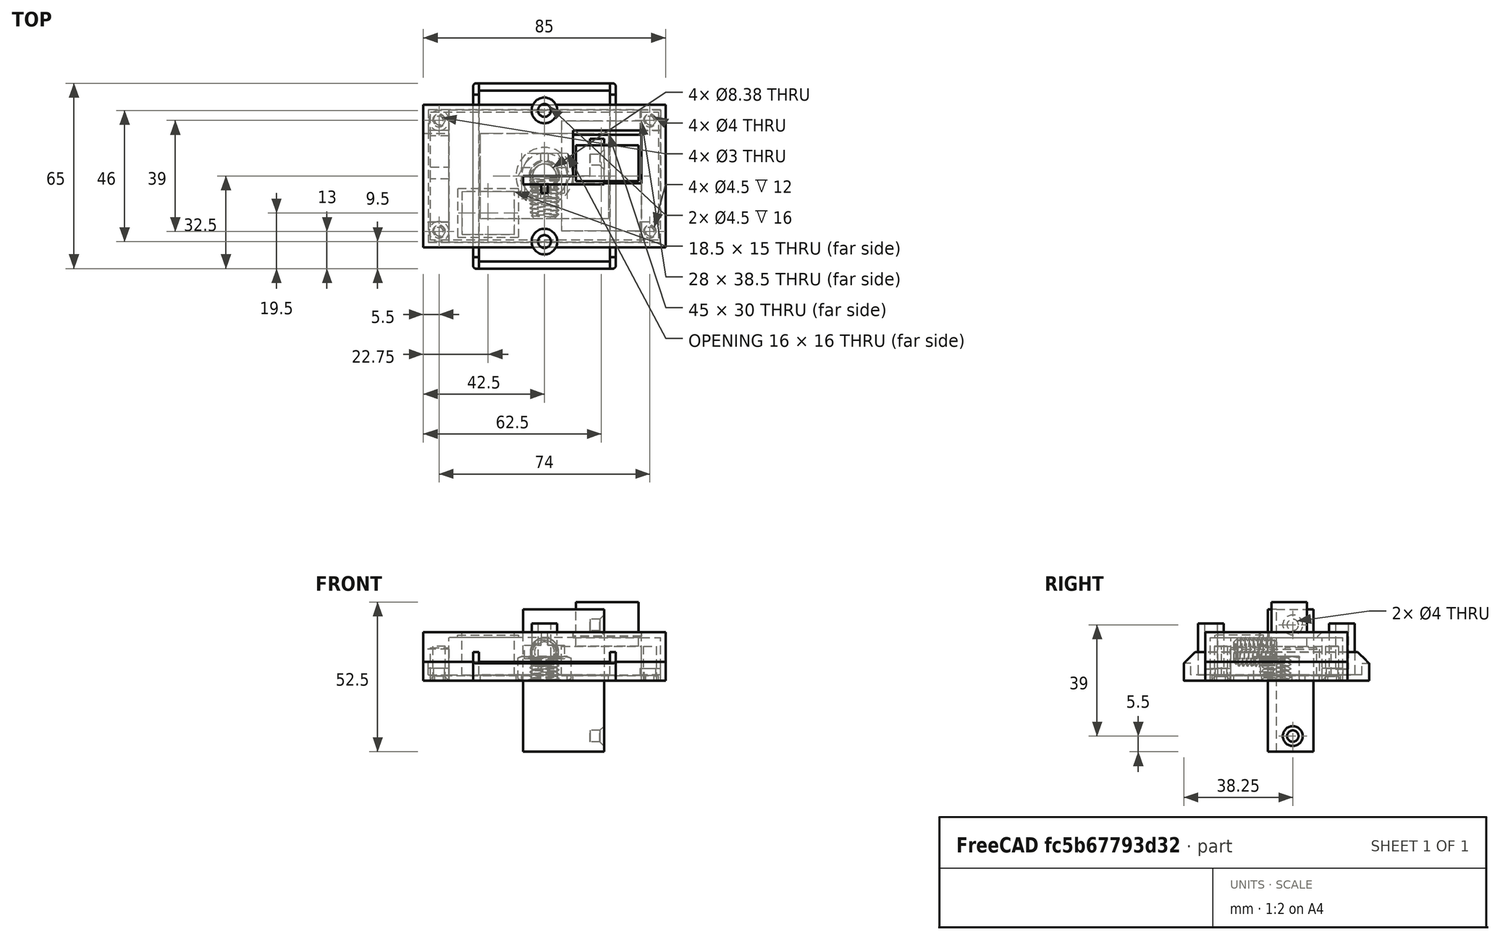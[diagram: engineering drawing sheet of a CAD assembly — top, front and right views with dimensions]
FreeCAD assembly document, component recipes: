
FREECAD ASSEMBLY — COMPONENT RECIPES ("case")

This assembly document has 6 components, labeled P0..P5 below (a component is one placed body or linked part). 6 of them carry a construction recipe — the FreeCAD feature program that regenerates the part from scratch, quoted from this document or its linked companion documents; the rest are supplied as boundary geometry only. No exploded tour is included for this assembly.
COMPONENT P0 — recipe-attached ("Base", modeled in this document).
Construction recipe (the document's own serialized feature program — sketch geometry with constraints, then the solid features built on it; lengths are millimeters unless a unit is written):

FEATURE [PartDesign::CoordinateSystem] LCS_002
  AttacherType = Attacher::AttachEngine3D
  MapMode = 2
  Support = -> [X_Axis003]
FEATURE [Sketcher::SketchObject] Sketch007
  FullyConstrained = true
  MapMode = 5
  Support = -> [XY_Plane003]
  sketch-geometry (4):
    g0: LineSegment StartX=-42.5 StartY=25 StartZ=0 EndX=42.5 EndY=25 EndZ=0
    g1: LineSegment StartX=42.5 StartY=25 StartZ=0 EndX=42.5 EndY=-25 EndZ=0
    g2: LineSegment StartX=42.5 StartY=-25 StartZ=0 EndX=-42.5 EndY=-25 EndZ=0
    g3: LineSegment StartX=-42.5 StartY=-25 StartZ=0 EndX=-42.5 EndY=25 EndZ=0
  constraints (10):
    c: Horizontal(g0)
    c: Vertical(g1)
    c: Coincident(g2,g1)
    c: Coincident(g3,g2)
    c: Coincident(g0,g3)
    c: DistanceX(g2,g2) = 85
    c: DistanceY(g3,g3) = 50
    c: Symmetric(g1,g2,g-2)
    c: Symmetric(g0,g2,g-1)
    c: Coincident(g0,g1)
FEATURE [PartDesign::Pad] Pad006
  Direction = (0,0,1)
  Length = 6.5
  Length2 = 10
  Profile = -> Sketch007
  ReferenceAxis = -> Sketch007 [N_Axis]
  Type = 0
FEATURE [PartDesign::CoordinateSystem] Local_CS004  label="MainboardMount"
  AttacherType = Attacher::AttachEngine3D
  AttachmentOffset = pos=(0,0,4.5) rot=(0,0,1;0rad)
  MapMode = 5
  Placement = pos=(0,0,4.5) rot=(0,0,1;0rad)
  Support = -> [LCS_002]
FEATURE [Sketcher::SketchObject] Sketch008
  AttachmentOffset = pos=(0,0,2) rot=(0,0,1;0rad)
  FullyConstrained = true
  MapMode = 5
  Placement = pos=(0,0,2) rot=(0,0,1;0rad)
  Support = -> [XY_Plane003]
  sketch-geometry (4):
    g0: LineSegment StartX=-40.75 StartY=23.25 StartZ=0 EndX=40.75 EndY=23.25 EndZ=0
    g1: LineSegment StartX=40.75 StartY=23.25 StartZ=0 EndX=40.75 EndY=-23.25 EndZ=0
    g2: LineSegment StartX=40.75 StartY=-23.25 StartZ=0 EndX=-40.75 EndY=-23.25 EndZ=0
    g3: LineSegment StartX=-40.75 StartY=-23.25 StartZ=0 EndX=-40.75 EndY=23.25 EndZ=0
  constraints (10):
    c: Coincident(g0,g1)
    c: Coincident(g1,g2)
    c: Coincident(g2,g3)
    c: Coincident(g3,g0)
    c: Horizontal(g2)
    c: Vertical(g3)
    c: DistanceX(g0,g0) = 81.5
    c: DistanceY(g1,g1) = 46.5
    c: Symmetric(g0,g1,g-1)
    c: Symmetric(g0,g0,g-2)
FEATURE [PartDesign::Pocket] Pocket
  BaseFeature = -> Pad006
  Direction = (0,0,-1)
  Length = 5
  Length2 = 5
  Profile = -> Sketch008
  ReferenceAxis = -> Sketch008 [N_Axis]
  Reversed = true
  Type = 1
FEATURE [Sketcher::SketchObject] Sketch010
  FullyConstrained = true
  MapMode = 5
  Support = -> [XY_Plane003]
  sketch-geometry (4):
    g0: LineSegment StartX=-33.5 StartY=-16 StartZ=0 EndX=-42.5 EndY=-16 EndZ=0
    g1: LineSegment StartX=-42.5 StartY=-16 StartZ=0 EndX=-42.5 EndY=-25 EndZ=0
    g2: LineSegment StartX=-42.5 StartY=-25 StartZ=0 EndX=-33.5 EndY=-25 EndZ=0
    g3: LineSegment StartX=-33.5 StartY=-25 StartZ=0 EndX=-33.5 EndY=-16 EndZ=0
  constraints (12):
    c: Coincident(g0,g1)
    c: Coincident(g1,g2)
    c: Coincident(g2,g3)
    c: Coincident(g3,g0)
    c: Horizontal(g0)
    c: Horizontal(g2)
    c: Vertical(g1)
    c: Vertical(g3)
    c: DistanceX(g0,g-1) = 33.5
    c: DistanceY(g0,g-1) = 16
    c: DistanceX(g2,g2) = 9
    c: DistanceY(g1,g1) = 9
FEATURE [PartDesign::Pad] Pad007
  BaseFeature = -> Pocket
  Direction = (0,0,1)
  Length = 4.3
  Length2 = 10
  Profile = -> Sketch010
  ReferenceAxis = -> Sketch010 [N_Axis]
  Type = 0
FEATURE [PartDesign::Mirrored] Mirrored002
  MirrorPlane = -> Sketch010 [V_Axis]
FEATURE [PartDesign::Mirrored] Mirrored003
  MirrorPlane = -> Sketch010 [H_Axis]
FEATURE [PartDesign::MultiTransform] MultiTransform001
  BaseFeature = -> Pad007
  Originals = -> [Pad007]
  Transformations = -> [Mirrored002,Mirrored003]
FEATURE [PartDesign::SubtractiveCylinder] Cylinder001
  Angle = 360
  AttacherType = Attacher::AttachEngine3D
  AttachmentOffset = pos=(-37,-19.5,0) rot=(0,0,1;0rad)
  BaseFeature = -> MultiTransform001
  FirstAngle = 0
  Height = 10
  MapMode = 5
  Placement = pos=(-37,-19.5,0) rot=(0,0,1;0rad)
  Radius = 2
  SecondAngle = 0
  Support = -> [XY_Plane003]
  expr: Radius = 2
FEATURE [PartDesign::Mirrored] Mirrored004
  MirrorPlane = -> YZ_Plane003
  Placement = pos=(-37,-19.5,0) rot=(0,0,1;0rad)
FEATURE [PartDesign::Mirrored] Mirrored005
  MirrorPlane = -> XZ_Plane003
  Placement = pos=(-37,-19.5,0) rot=(0,0,1;0rad)
FEATURE [PartDesign::MultiTransform] MultiTransform002
  BaseFeature = -> Cylinder001
  Originals = -> [Cylinder001]
  Placement = pos=(-37,-19.5,0) rot=(0,0,1;0rad)
  Transformations = -> [Mirrored004,Mirrored005]
FEATURE [PartDesign::CoordinateSystem] Local_CS006  label="TopMount"
  AttacherType = Attacher::AttachEngine3D
  AttachmentOffset = pos=(0,0,6.5) rot=(0,0,1;0rad)
  MapMode = 5
  Placement = pos=(0,0,6.5) rot=(0,0,1;0rad)
  Support = -> [LCS_002]
FEATURE [Sketcher::SketchObject] Sketch017
  AttachmentOffset = pos=(0,0,6.5) rot=(0,0,1;0rad)
  FullyConstrained = false
  MapMode = 5
  Placement = pos=(0,0,6.5) rot=(0,0,1;0rad)
  Support = -> [XY_Plane003]
  sketch-geometry (4):
    g0: LineSegment StartX=-43.7107 StartY=16 StartZ=0 EndX=-39.4081 EndY=16 EndZ=0
    g1: LineSegment StartX=-39.4081 StartY=16 StartZ=0 EndX=-39.4081 EndY=-16 EndZ=0
    g2: LineSegment StartX=-39.4081 StartY=-16 StartZ=0 EndX=-43.7107 EndY=-16 EndZ=0
    g3: LineSegment StartX=-43.7107 StartY=-16 StartZ=0 EndX=-43.7107 EndY=16 EndZ=0
  constraints (9):
    c: Coincident(g0,g1)
    c: Coincident(g1,g2)
    c: Coincident(g2,g3)
    c: Coincident(g3,g0)
    c: Horizontal(g0)
    c: Horizontal(g2)
    c: Vertical(g1)
    c: DistanceY(g3,g3) = 32
    c: Symmetric(g0,g2,g-1)
FEATURE [PartDesign::Pocket] Pocket006
  BaseFeature = -> MultiTransform002
  Direction = (0,0,-1)
  Length = 5
  Length2 = 5
  Placement = pos=(-37,-19.5,0) rot=(0,0,1;0rad)
  Profile = -> Sketch017
  ReferenceAxis = -> Sketch017 [N_Axis]
  Reversed = true
  Type = 0
FEATURE [PartDesign::Chamfer] Chamfer
  Angle = 45
  Base = -> Pocket006 [Edge62,Edge8]
  BaseFeature = -> Pocket006
  ChamferType = 0
  FlipDirection = false
  Placement = pos=(-37,-19.5,0) rot=(0,0,1;0rad)
  Size = 1.5
  Size2 = 1
  SupportTransform = false
  UseAllEdges = false
FEATURE [PartDesign::CoordinateSystem] Local_CS008  label="ScrewBase"
  AttacherType = Attacher::AttachEngine3D
  AttachmentOffset = pos=(-1,2,0) rot=(0,0,1;0rad)
  MapMode = 45
  Placement = pos=(43.5,4e-16,2) rot=(0,0.707107,0.707107;3.14159rad)
  Support = -> [Chamfer]
FEATURE [PartDesign::Body] Base
  Group = -> [LCS_002,Sketch007,Pad006,Local_CS004,Sketch008,Sketch010,Pocket,Pad007,MultiTransform001,Mirrored002,Mirrored003,Cylinder001,MultiTransform002,Mirrored004,Mirrored005,Local_CS006,Sketch017,Pocket006,Local_CS008,Chamfer]
  Origin = -> Origin003
  Tip = -> Chamfer
COMPONENT P1 — recipe-attached ("Mainboard", modeled in this document).
Construction recipe (the document's own serialized feature program — sketch geometry with constraints, then the solid features built on it; lengths are millimeters unless a unit is written):

FEATURE [PartDesign::CoordinateSystem] LCS_0
  AttacherType = Attacher::AttachEngine3D
  MapMode = 2
  Support = -> [X_Axis001]
FEATURE [Sketcher::SketchObject] Sketch
  FullyConstrained = true
  MapMode = 5
  Support = -> [XY_Plane001]
  sketch-geometry (4):
    g0: LineSegment StartX=-40 StartY=22.5 StartZ=0 EndX=40 EndY=22.5 EndZ=0
    g1: LineSegment StartX=40 StartY=22.5 StartZ=0 EndX=40 EndY=-22.5 EndZ=0
    g2: LineSegment StartX=40 StartY=-22.5 StartZ=0 EndX=-40 EndY=-22.5 EndZ=0
    g3: LineSegment StartX=-40 StartY=-22.5 StartZ=0 EndX=-40 EndY=22.5 EndZ=0
  constraints (10):
    c: Coincident(g0,g1)
    c: Coincident(g1,g2)
    c: Coincident(g2,g3)
    c: Coincident(g3,g0)
    c: Horizontal(g2)
    c: Vertical(g1)
    c: DistanceX(g0,g0) = 80
    c: DistanceY(g3,g3) = 45
    c: Symmetric(g0,g2,g-1)
    c: Symmetric(g0,g0,g-2)
FEATURE [PartDesign::Pad] Pad
  Direction = (0,0,1)
  Length = 1.7
  Length2 = 10
  Profile = -> Sketch
  ReferenceAxis = -> Sketch [N_Axis]
  Type = 0
FEATURE [Sketcher::SketchObject] Sketch001
  FullyConstrained = true
  MapMode = 5
  Support = -> [XY_Plane001]
  expr: Constraints[11] = 45 / 2 - 8.4
  sketch-geometry (4):
    g0: LineSegment StartX=-40 StartY=14.1 StartZ=0 EndX=-33.5 EndY=14.1 EndZ=0
    g1: LineSegment StartX=-33.5 StartY=14.1 StartZ=0 EndX=-33.5 EndY=3.1 EndZ=0
    g2: LineSegment StartX=-33.5 StartY=3.1 StartZ=0 EndX=-40 EndY=3.1 EndZ=0
    g3: LineSegment StartX=-40 StartY=3.1 StartZ=0 EndX=-40 EndY=14.1 EndZ=0
  constraints (12):
    c: Coincident(g0,g1)
    c: Coincident(g1,g2)
    c: Coincident(g2,g3)
    c: Coincident(g3,g0)
    c: Horizontal(g0)
    c: Horizontal(g2)
    c: Vertical(g1)
    c: Vertical(g3)
    c: DistanceY(g1,g1) = 11
    c: DistanceX(g0,g0) = 6.5
    c: DistanceX(g0,g-1) = 40
    c: DistanceY(g-1,g0) = 14.1
FEATURE [PartDesign::Pad] Pad001
  BaseFeature = -> Pad
  Direction = (0,0,1)
  Length = 11.5
  Length2 = 10
  Profile = -> Sketch001
  ReferenceAxis = -> Sketch001 [N_Axis]
  Type = 0
FEATURE [Sketcher::SketchObject] Sketch002
  FullyConstrained = true
  MapMode = 5
  Support = -> [XY_Plane001]
  expr: Constraints[11] = 45 / 2 - 6.5
  sketch-geometry (4):
    g0: LineSegment StartX=-40 StartY=-1 StartZ=0 EndX=-33.5 EndY=-1 EndZ=0
    g1: LineSegment StartX=-33.5 StartY=-1 StartZ=0 EndX=-33.5 EndY=-16 EndZ=0
    g2: LineSegment StartX=-33.5 StartY=-16 StartZ=0 EndX=-40 EndY=-16 EndZ=0
    g3: LineSegment StartX=-40 StartY=-16 StartZ=0 EndX=-40 EndY=-1 EndZ=0
  constraints (12):
    c: Coincident(g0,g1)
    c: Coincident(g1,g2)
    c: Coincident(g2,g3)
    c: Coincident(g3,g0)
    c: Horizontal(g0)
    c: Horizontal(g2)
    c: Vertical(g1)
    c: Vertical(g3)
    c: DistanceX(g0,g0) = 6.5
    c: DistanceY(g3,g3) = 15
    c: DistanceX(g0,g-1) = 40
    c: DistanceY(g2,g-1) = 16
FEATURE [PartDesign::Pad] Pad002
  BaseFeature = -> Pad001
  Direction = (0,0,1)
  Length = 11.5
  Length2 = 10
  Profile = -> Sketch002
  ReferenceAxis = -> Sketch002 [N_Axis]
  Type = 0
FEATURE [Sketcher::SketchObject] Sketch003
  FullyConstrained = true
  MapMode = 5
  Support = -> [XY_Plane001]
  expr: Constraints[10] = 40 - 11
  expr: Constraints[11] = 45 / 2 - 2
  sketch-geometry (4):
    g0: LineSegment StartX=-29 StartY=-5.5 StartZ=0 EndX=-10.5 EndY=-5.5 EndZ=0
    g1: LineSegment StartX=-10.5 StartY=-5.5 StartZ=0 EndX=-10.5 EndY=-20.5 EndZ=0
    g2: LineSegment StartX=-10.5 StartY=-20.5 StartZ=0 EndX=-29 EndY=-20.5 EndZ=0
    g3: LineSegment StartX=-29 StartY=-20.5 StartZ=0 EndX=-29 EndY=-5.5 EndZ=0
  constraints (12):
    c: Coincident(g0,g1)
    c: Coincident(g1,g2)
    c: Coincident(g2,g3)
    c: Coincident(g3,g0)
    c: Horizontal(g0)
    c: Horizontal(g2)
    c: Vertical(g1)
    c: Vertical(g3)
    c: DistanceX(g0,g0) = 18.5
    c: DistanceY(g3,g3) = 15
    c: DistanceX(g2,g-1) = 29
    c: DistanceY(g2,g-1) = 20.5
FEATURE [PartDesign::Pad] Pad003
  BaseFeature = -> Pad002
  Direction = (0,0,1)
  Length = 16.8
  Length2 = 10
  Profile = -> Sketch003
  ReferenceAxis = -> Sketch003 [N_Axis]
  Type = 0
FEATURE [PartDesign::SubtractiveCylinder] Cylinder
  Angle = 360
  AttacherType = Attacher::AttachEngine3D
  AttachmentOffset = pos=(37,19.5,0) rot=(0,0,1;0rad)
  BaseFeature = -> Pad003
  FirstAngle = 0
  Height = 10
  MapMode = 5
  Placement = pos=(37,19.5,0) rot=(0,0,1;0rad)
  Radius = 1.5
  SecondAngle = 0
  Support = -> [XY_Plane001]
  expr: .AttachmentOffset.Base.x = 40 - 3
  expr: .AttachmentOffset.Base.y = 45 / 2 - 3
FEATURE [PartDesign::Mirrored] Mirrored
  MirrorPlane = -> YZ_Plane001
  Placement = pos=(37,19.5,0) rot=(0,0,1;0rad)
FEATURE [PartDesign::Mirrored] Mirrored001
  MirrorPlane = -> XZ_Plane001
  Placement = pos=(37,19.5,0) rot=(0,0,1;0rad)
FEATURE [PartDesign::MultiTransform] MultiTransform
  BaseFeature = -> Cylinder
  Originals = -> [Cylinder]
  Placement = pos=(37,19.5,0) rot=(0,0,1;0rad)
  Transformations = -> [Mirrored,Mirrored001]
FEATURE [PartDesign::CoordinateSystem] Local_CS001  label="BottomLeft001"
  AttacherType = Attacher::AttachEngine3D
  MapMode = 1
  Placement = pos=(-40,-22.5,0) rot=(0,0,1;0rad)
  Support = -> [MultiTransform]
FEATURE [PartDesign::CoordinateSystem] Local_CS003  label="TopRight"
  AttacherType = Attacher::AttachEngine3D
  MapMode = 1
  Placement = pos=(40,22.5,0) rot=(0,0,1;0rad)
  Support = -> [MultiTransform]
FEATURE [Sketcher::SketchObject] Sketch034
  FullyConstrained = true
  MapMode = 5
  Support = -> [XY_Plane001]
  sketch-geometry (4):
    g0: LineSegment StartX=6 StartY=19.25 StartZ=0 EndX=34 EndY=19.25 EndZ=0
    g1: LineSegment StartX=34 StartY=19.25 StartZ=0 EndX=34 EndY=-19.25 EndZ=0
    g2: LineSegment StartX=34 StartY=-19.25 StartZ=0 EndX=6 EndY=-19.25 EndZ=0
    g3: LineSegment StartX=6 StartY=-19.25 StartZ=0 EndX=6 EndY=19.25 EndZ=0
  constraints (11):
    c: Coincident(g0,g1)
    c: Coincident(g1,g2)
    c: Coincident(g2,g3)
    c: Coincident(g3,g0)
    c: Horizontal(g0)
    c: Horizontal(g2)
    c: Vertical(g1)
    c: DistanceX(g0,g0) = 28
    c: DistanceY(g1,g1) = 38.5
    c: Symmetric(g0,g2,g-1)
    c: DistanceX(g-1,g0) = 34
FEATURE [PartDesign::Pad] Pad017
  BaseFeature = -> MultiTransform
  Direction = (0,0,1)
  Length = 12
  Length2 = 10
  Placement = pos=(37,19.5,0) rot=(0,0,1;0rad)
  Profile = -> Sketch034
  ReferenceAxis = -> Sketch034 [N_Axis]
  Type = 0
FEATURE [PartDesign::CoordinateSystem] Local_CS009
  AttacherType = Attacher::AttachEngine3D
  AttachmentOffset = pos=(14.75,0,-16) rot=(0,0,1;0rad)
  MapMode = 7
  Placement = pos=(22,4.5,12) rot=(0.57735,-0.57735,-0.57735;2.0944rad)
  Support = -> [Pad017]
  expr: .AttachmentOffset.Base.x = 8.5 + 12.5 / 2
  expr: .AttachmentOffset.Base.z = -5 - 22 / 2
FEATURE [Sketcher::SketchObject] Sketch035
  AttachmentOffset = pos=(0,0,0) rot=(0,0,1;1.5708rad)
  FullyConstrained = true
  MapMode = 3
  Placement = pos=(22,4.5,12) rot=(0,-1,0;3.14159rad)
  Support = -> [Local_CS009]
  sketch-geometry (4):
    g0: LineSegment StartX=-11 StartY=6.25 StartZ=0 EndX=11 EndY=6.25 EndZ=0
    g1: LineSegment StartX=11 StartY=6.25 StartZ=0 EndX=11 EndY=-6.25 EndZ=0
    g2: LineSegment StartX=11 StartY=-6.25 StartZ=0 EndX=-11 EndY=-6.25 EndZ=0
    g3: LineSegment StartX=-11 StartY=-6.25 StartZ=0 EndX=-11 EndY=6.25 EndZ=0
  constraints (10):
    c: Coincident(g0,g1)
    c: Coincident(g1,g2)
    c: Coincident(g2,g3)
    c: Coincident(g3,g0)
    c: Horizontal(g2)
    c: Vertical(g1)
    c: DistanceX(g0,g0) = 22
    c: DistanceY(g3,g3) = 12.5
    c: Symmetric(g2,g0,g-1)
    c: Symmetric(g0,g0,g-2)
FEATURE [PartDesign::Pad] Pad018
  BaseFeature = -> Pad017
  Direction = (0,0,-1)
  Length = 15.5
  Length2 = 10
  Placement = pos=(37,19.5,0) rot=(0,0,1;0rad)
  Profile = -> Sketch035
  ReferenceAxis = -> Sketch035 [N_Axis]
  Reversed = true
  Type = 0
  expr: Length = 15.5
FEATURE [PartDesign::Body] Mainboard
  Group = -> [LCS_0,Sketch,Pad,Sketch001,Pad001,Sketch002,Pad002,Sketch003,Pad003,Cylinder,MultiTransform,Mirrored,Mirrored001,Local_CS001,Local_CS003,Sketch034,Pad017,Local_CS009,Sketch035,Pad018]
  Origin = -> Origin001
  Tip = -> Pad018
COMPONENT P2 — recipe-attached ("SSR_Cover", modeled in this document).
Construction recipe (the document's own serialized feature program — sketch geometry with constraints, then the solid features built on it; lengths are millimeters unless a unit is written):

FEATURE [PartDesign::CoordinateSystem] LCS_005
  AttacherType = Attacher::AttachEngine3D
  MapMode = 2
  Support = -> [X_Axis006]
FEATURE [Sketcher::SketchObject] Sketch025
  FullyConstrained = true
  MapMode = 5
  Support = -> [XY_Plane006]
  sketch-geometry (4):
    g0: LineSegment StartX=-25 StartY=32.5 StartZ=0 EndX=25 EndY=32.5 EndZ=0
    g1: LineSegment StartX=25 StartY=32.5 StartZ=0 EndX=25 EndY=-32.5 EndZ=0
    g2: LineSegment StartX=25 StartY=-32.5 StartZ=0 EndX=-25 EndY=-32.5 EndZ=0
    g3: LineSegment StartX=-25 StartY=-32.5 StartZ=0 EndX=-25 EndY=32.5 EndZ=0
  constraints (10):
    c: Coincident(g0,g1)
    c: Coincident(g1,g2)
    c: Coincident(g2,g3)
    c: Coincident(g3,g0)
    c: Horizontal(g0)
    c: Vertical(g1)
    c: DistanceX(g0,g0) = 50
    c: DistanceY(g3,g3) = 65
    c: Symmetric(g2,g1,g-2)
    c: Symmetric(g0,g2,g-1)
FEATURE [PartDesign::Pad] Pad015
  Direction = (0,0,1)
  Length = 10
  Length2 = 10
  Profile = -> Sketch025
  ReferenceAxis = -> Sketch025 [N_Axis]
  Type = 0
FEATURE [Sketcher::SketchObject] Sketch026
  FullyConstrained = true
  MapMode = 5
  Support = -> [XY_Plane006]
  sketch-geometry (4):
    g0: LineSegment StartX=-22.5 StartY=15 StartZ=0 EndX=22.5 EndY=15 EndZ=0
    g1: LineSegment StartX=22.5 StartY=15 StartZ=0 EndX=22.5 EndY=-15 EndZ=0
    g2: LineSegment StartX=22.5 StartY=-15 StartZ=0 EndX=-22.5 EndY=-15 EndZ=0
    g3: LineSegment StartX=-22.5 StartY=-15 StartZ=0 EndX=-22.5 EndY=15 EndZ=0
  constraints (10):
    c: Coincident(g0,g1)
    c: Coincident(g1,g2)
    c: Coincident(g2,g3)
    c: Coincident(g3,g0)
    c: Horizontal(g0)
    c: Vertical(g1)
    c: DistanceX(g0,g0) = 45
    c: DistanceY(g3,g3) = 30
    c: Symmetric(g2,g0,g-1)
    c: Symmetric(g1,g2,g-2)
FEATURE [PartDesign::Pocket] Pocket008
  BaseFeature = -> Pad015
  Direction = (0,0,-1)
  Length = 5
  Length2 = 5
  Profile = -> Sketch026
  ReferenceAxis = -> Sketch026 [N_Axis]
  Reversed = true
  Type = 1
FEATURE [Sketcher::SketchObject] Sketch027
  AttachmentOffset = pos=(0,0,2) rot=(0,0,1;0rad)
  FullyConstrained = true
  MapMode = 5
  Placement = pos=(0,0,2) rot=(0,0,1;0rad)
  Support = -> [XY_Plane006]
  sketch-geometry (4):
    g0: LineSegment StartX=-23 StartY=30 StartZ=0 EndX=23 EndY=30 EndZ=0
    g1: LineSegment StartX=23 StartY=30 StartZ=0 EndX=23 EndY=-30 EndZ=0
    g2: LineSegment StartX=23 StartY=-30 StartZ=0 EndX=-23 EndY=-30 EndZ=0
    g3: LineSegment StartX=-23 StartY=-30 StartZ=0 EndX=-23 EndY=30 EndZ=0
  constraints (10):
    c: Coincident(g0,g1)
    c: Coincident(g1,g2)
    c: Coincident(g2,g3)
    c: Coincident(g3,g0)
    c: Horizontal(g2)
    c: Vertical(g1)
    c: DistanceX(g0,g0) = 46
    c: DistanceY(g3,g3) = 60
    c: Symmetric(g0,g2,g-1)
    c: Symmetric(g0,g0,g-2)
FEATURE [PartDesign::Pocket] Pocket009
  BaseFeature = -> Pocket008
  Direction = (0,0,-1)
  Length = 5
  Length2 = 5
  Profile = -> Sketch027
  ReferenceAxis = -> Sketch027 [N_Axis]
  Reversed = true
  Type = 1
FEATURE [Sketcher::SketchObject] Sketch028
  AttachmentOffset = pos=(0,0,6) rot=(0,0,1;0rad)
  FullyConstrained = true
  MapMode = 5
  Placement = pos=(0,0,6) rot=(0,0,1;0rad)
  Support = -> [XY_Plane006]
  sketch-geometry (4):
    g0: LineSegment StartX=-23 StartY=50 StartZ=0 EndX=23 EndY=50 EndZ=0
    g1: LineSegment StartX=23 StartY=50 StartZ=0 EndX=23 EndY=-50 EndZ=0
    g2: LineSegment StartX=23 StartY=-50 StartZ=0 EndX=-23 EndY=-50 EndZ=0
    g3: LineSegment StartX=-23 StartY=-50 StartZ=0 EndX=-23 EndY=50 EndZ=0
  constraints (10):
    c: Coincident(g0,g1)
    c: Coincident(g1,g2)
    c: Coincident(g2,g3)
    c: Coincident(g3,g0)
    c: Horizontal(g2)
    c: Vertical(g1)
    c: DistanceX(g0,g0) = 46
    c: DistanceY(g3,g3) = 100
    c: Symmetric(g0,g2,g-1)
    c: Symmetric(g0,g0,g-2)
FEATURE [PartDesign::Pocket] Pocket010
  BaseFeature = -> Pocket009
  Direction = (0,0,-1)
  Length = 5
  Length2 = 5
  Profile = -> Sketch028
  ReferenceAxis = -> Sketch028 [N_Axis]
  Reversed = true
  Type = 0
FEATURE [PartDesign::Chamfer] Chamfer002
  Angle = 45
  Base = -> Pocket010 [Edge30,Edge18,Edge3,Edge7]
  BaseFeature = -> Pocket010
  ChamferType = 0
  FlipDirection = false
  Size = 4
  Size2 = 1
  SupportTransform = false
  UseAllEdges = false
FEATURE [PartDesign::Fillet] Fillet
  Base = -> Chamfer002 [Edge1,Edge10,Edge5,Edge24]
  BaseFeature = -> Chamfer002
  Radius = 1
  SupportTransform = false
  UseAllEdges = false
FEATURE [PartDesign::AdditiveCylinder] Cylinder004
  Angle = 360
  AttacherType = Attacher::AttachEngine3D
  AttachmentOffset = pos=(0,23,0) rot=(0,0,1;0rad)
  BaseFeature = -> Fillet
  FirstAngle = 0
  Height = 20
  MapMode = 5
  Placement = pos=(0,23,0) rot=(0,0,1;0rad)
  Radius = 4.5
  SecondAngle = 0
  Support = -> [XY_Plane006]
FEATURE [PartDesign::SubtractiveCylinder] Cylinder005
  Angle = 360
  AttacherType = Attacher::AttachEngine3D
  AttachmentOffset = pos=(0,23,4) rot=(0,0,1;0rad)
  BaseFeature = -> Cylinder004
  FirstAngle = 0
  Height = 20
  MapMode = 5
  Placement = pos=(0,23,4) rot=(0,0,1;0rad)
  Radius = 2.25
  SecondAngle = 0
  Support = -> [XY_Plane006]
  expr: Radius = 4.5 / 2
FEATURE [PartDesign::Mirrored] Mirrored012
  BaseFeature = -> Cylinder005
  MirrorPlane = -> XZ_Plane006
  Originals = -> [Cylinder004,Cylinder005]
  Placement = pos=(0,23,4) rot=(0,0,1;0rad)
FEATURE [PartDesign::Body] SSR_Cover
  Group = -> [LCS_005,Sketch025,Pad015,Sketch026,Pocket008,Sketch027,Pocket009,Sketch028,Pocket010,Chamfer002,Fillet,Cylinder004,Cylinder005,Mirrored012]
  Origin = -> Origin006
  Tip = -> Mirrored012
COMPONENT P3 — recipe-attached ("Top", modeled in this document).
Construction recipe (the document's own serialized feature program — sketch geometry with constraints, then the solid features built on it; lengths are millimeters unless a unit is written):

FEATURE [PartDesign::CoordinateSystem] LCS_003
  AttacherType = Attacher::AttachEngine3D
  MapMode = 2
  Support = -> [X_Axis004]
FEATURE [Sketcher::SketchObject] Sketch012
  FullyConstrained = true
  MapMode = 5
  Support = -> [XY_Plane004]
  sketch-geometry (4):
    g0: LineSegment StartX=-42.5 StartY=25 StartZ=0 EndX=42.5 EndY=25 EndZ=0
    g1: LineSegment StartX=42.5 StartY=25 StartZ=0 EndX=42.5 EndY=-25 EndZ=0
    g2: LineSegment StartX=42.5 StartY=-25 StartZ=0 EndX=-42.5 EndY=-25 EndZ=0
    g3: LineSegment StartX=-42.5 StartY=-25 StartZ=0 EndX=-42.5 EndY=25 EndZ=0
  constraints (10):
    c: Horizontal(g0)
    c: Vertical(g1)
    c: Coincident(g2,g1)
    c: Coincident(g3,g2)
    c: Coincident(g0,g3)
    c: DistanceX(g2,g2) = 85
    c: DistanceY(g3,g3) = 50
    c: Symmetric(g1,g2,g-2)
    c: Symmetric(g0,g2,g-1)
    c: Coincident(g1,g0)
FEATURE [PartDesign::Pad] Pad009
  Direction = (0,0,1)
  Length = 17
  Length2 = 10
  Profile = -> Sketch012
  ReferenceAxis = -> Sketch012 [N_Axis]
  Type = 0
FEATURE [Sketcher::SketchObject] Sketch013
  FullyConstrained = false
  MapMode = 5
  Support = -> [XY_Plane004]
  sketch-geometry (4):
    g0: LineSegment StartX=-46.463 StartY=15 StartZ=0 EndX=-31.5928 EndY=15 EndZ=0
    g1: LineSegment StartX=-31.5928 StartY=15 StartZ=0 EndX=-31.5928 EndY=-16.25 EndZ=0
    g2: LineSegment StartX=-31.5928 StartY=-16.25 StartZ=0 EndX=-46.463 EndY=-16.25 EndZ=0
    g3: LineSegment StartX=-46.463 StartY=-16.25 StartZ=0 EndX=-46.463 EndY=15 EndZ=0
  constraints (9):
    c: Coincident(g0,g1)
    c: Coincident(g1,g2)
    c: Coincident(g2,g3)
    c: Horizontal(g0)
    c: Horizontal(g2)
    c: Vertical(g1)
    c: DistanceY(g-1,g0) = 15
    c: DistanceY(g2,g-1) = 16.25
    c: Coincident(g3,g0)
FEATURE [PartDesign::Pocket] Pocket002
  BaseFeature = -> Pad009
  Direction = (0,0,-1)
  Length = 11
  Length2 = 5
  Profile = -> Sketch013
  ReferenceAxis = -> Sketch013 [N_Axis]
  Reversed = true
  Type = 0
FEATURE [Sketcher::SketchObject] Sketch014
  FullyConstrained = false
  MapMode = 5
  Support = -> [XY_Plane004]
  sketch-geometry (8):
    g0: LineSegment StartX=-33.4749 StartY=23.25 StartZ=0 EndX=34 EndY=23.25 EndZ=0
    g1: LineSegment StartX=34 StartY=-23.25 StartZ=0 EndX=-33.4749 EndY=-23.25 EndZ=0
    g2: LineSegment StartX=-33.4749 StartY=-23.25 StartZ=0 EndX=-33.4749 EndY=23.25 EndZ=0
    g3: LineSegment StartX=34 StartY=-23.25 StartZ=0 EndX=34 EndY=-16 EndZ=0
    g4: LineSegment StartX=34 StartY=-16 StartZ=0 EndX=40.75 EndY=-16 EndZ=0
    g5: LineSegment StartX=40.75 StartY=-16 StartZ=0 EndX=40.75 EndY=16 EndZ=0
    g6: LineSegment StartX=40.75 StartY=16 StartZ=0 EndX=34 EndY=16 EndZ=0
    g7: LineSegment StartX=34 StartY=16 StartZ=0 EndX=34 EndY=23.25 EndZ=0
  constraints (22):
    c: Coincident(g1,g2)
    c: Coincident(g2,g0)
    c: Horizontal(g0)
    c: Horizontal(g1)
    c: Vertical(g2)
    c: Coincident(g3,g1)
    c: Coincident(g4,g3)
    c: Horizontal(g4)
    c: Coincident(g5,g4)
    c: Coincident(g6,g5)
    c: Horizontal(g6)
    c: Coincident(g7,g6)
    c: Coincident(g7,g0)
    c: DistanceY(g2,g2) = 46.5
    c: DistanceX(g4,g4) = 6.75
    c: Vertical(g1,g3)
    c: Vertical(g3,g6)
    c: Vertical(g6,g0)
    c: DistanceY(g7,g7) = 7.25
    c: DistanceY(g3,g3) = 7.25
    c: Symmetric(g5,g4,g-1)
    c: DistanceX(g-1,g3) = 34
FEATURE [PartDesign::Pocket] Pocket003
  BaseFeature = -> Pocket002
  Direction = (0,0,-1)
  Length = 15
  Length2 = 5
  Profile = -> Sketch014
  ReferenceAxis = -> Sketch014 [N_Axis]
  Reversed = true
  Type = 0
FEATURE [PartDesign::Mirrored] Mirrored009
  MirrorPlane = -> YZ_Plane004
  Placement = pos=(-37,19.5,0) rot=(0,0,1;0rad)
FEATURE [PartDesign::Mirrored] Mirrored010
  MirrorPlane = -> XZ_Plane004
  Placement = pos=(-37,19.5,0) rot=(0,0,1;0rad)
FEATURE [Sketcher::SketchObject] Sketch018
  FullyConstrained = true
  MapMode = 5
  Support = -> [XY_Plane004]
  sketch-geometry (4):
    g0: LineSegment StartX=-30.5 StartY=-4.5 StartZ=0 EndX=-9 EndY=-4.5 EndZ=0
    g1: LineSegment StartX=-9 StartY=-4.5 StartZ=0 EndX=-9 EndY=-21.5 EndZ=0
    g2: LineSegment StartX=-9 StartY=-21.5 StartZ=0 EndX=-30.5 EndY=-21.5 EndZ=0
    g3: LineSegment StartX=-30.5 StartY=-21.5 StartZ=0 EndX=-30.5 EndY=-4.5 EndZ=0
  constraints (12):
    c: Coincident(g0,g1)
    c: Coincident(g1,g2)
    c: Coincident(g2,g3)
    c: Coincident(g3,g0)
    c: Horizontal(g0)
    c: Horizontal(g2)
    c: Vertical(g1)
    c: Vertical(g3)
    c: DistanceX(g0,g-1) = 9
    c: DistanceX(g0,g0) = 21.5
    c: DistanceY(g1,g1) = 17
    c: DistanceY(g0,g-1) = 4.5
FEATURE [PartDesign::Pocket] Pocket007
  BaseFeature = -> Pocket003
  Direction = (0,0,-1)
  Length = 16
  Length2 = 5
  Profile = -> Sketch018
  ReferenceAxis = -> Sketch018 [N_Axis]
  Reversed = true
  Type = 0
FEATURE [PartDesign::SubtractiveCylinder] Cylinder002
  Angle = 360
  AttacherType = Attacher::AttachEngine3D
  AttachmentOffset = pos=(-37,19.5,0) rot=(0,0,1;0rad)
  BaseFeature = -> Pocket007
  FirstAngle = 0
  Height = 12
  MapMode = 5
  Placement = pos=(-37,19.5,0) rot=(0,0,1;0rad)
  Radius = 2.25
  SecondAngle = 0
  Support = -> [XY_Plane004]
  expr: Radius = 4.5 / 2
FEATURE [PartDesign::MultiTransform] MultiTransform004
  BaseFeature = -> Cylinder002
  Originals = -> [Cylinder002]
  Placement = pos=(-37,19.5,0) rot=(0,0,1;0rad)
  Transformations = -> [Mirrored009,Mirrored010]
FEATURE [Sketcher::SketchObject] Sketch036
  FullyConstrained = true
  MapMode = 5
  Support = -> [XY_Plane004]
FEATURE [Sketcher::SketchObject] Sketch037
  FullyConstrained = true
  MapMode = 5
  Support = -> [XY_Plane004]
  sketch-geometry (4):
    g0: LineSegment StartX=10 StartY=14.5 StartZ=0 EndX=34 EndY=14.5 EndZ=0
    g1: LineSegment StartX=34 StartY=14.5 StartZ=0 EndX=34 EndY=-2.5 EndZ=0
    g2: LineSegment StartX=34 StartY=-2.5 StartZ=0 EndX=10 EndY=-2.5 EndZ=0
    g3: LineSegment StartX=10 StartY=-2.5 StartZ=0 EndX=10 EndY=14.5 EndZ=0
  constraints (12):
    c: Coincident(g0,g1)
    c: Coincident(g1,g2)
    c: Coincident(g2,g3)
    c: Coincident(g3,g0)
    c: Horizontal(g0)
    c: Horizontal(g2)
    c: Vertical(g1)
    c: Vertical(g3)
    c: DistanceX(g0,g0) = 24
    c: DistanceY(g3,g3) = 17
    c: DistanceX(g-1,g0) = 10
    c: DistanceY(g2,g-1) = 2.5
FEATURE [PartDesign::Pocket] Pocket014
  BaseFeature = -> MultiTransform004
  Direction = (0,0,-1)
  Length = 5
  Length2 = 5
  Placement = pos=(-37,19.5,0) rot=(0,0,1;0rad)
  Profile = -> Sketch037
  ReferenceAxis = -> Sketch037 [N_Axis]
  Reversed = true
  Type = 1
FEATURE [PartDesign::Chamfer] Chamfer003
  Angle = 45
  Base = -> Pocket014 [Edge32]
  BaseFeature = -> Pocket014
  ChamferType = 0
  FlipDirection = false
  Placement = pos=(-37,19.5,0) rot=(0,0,1;0rad)
  Size = 1.5
  Size2 = 1
  SupportTransform = false
  UseAllEdges = false
FEATURE [PartDesign::Body] Top
  Group = -> [LCS_003,Sketch012,Pad009,Sketch013,Pocket002,Sketch014,Pocket003,Sketch018,Pocket007,Cylinder002,MultiTransform004,Mirrored009,Mirrored010,Sketch036,Sketch037,Pocket014,Chamfer003]
  Origin = -> Origin004
  Tip = -> Chamfer003
COMPONENT P4 — recipe-attached ("Washer", modeled in this document).
Construction recipe (the document's own serialized feature program — sketch geometry with constraints, then the solid features built on it; lengths are millimeters unless a unit is written):

FEATURE [PartDesign::CoordinateSystem] LCS_006
  AttacherType = Attacher::AttachEngine3D
  MapMode = 2
  Support = -> [X_Axis007]
FEATURE [Sketcher::SketchObject] Sketch030
  FullyConstrained = true
  MapMode = 5
  Support = -> [XY_Plane007]
  sketch-geometry (1):
    g0: Circle CenterX=0 CenterY=0 CenterZ=0 NormalX=0 NormalY=0 NormalZ=1 AngleXU=0 Radius=10
  constraints (2):
    c: Coincident(g0,g-1)
    c: Diameter(g0) = 20
FEATURE [PartDesign::Pad] Pad016
  Direction = (0,0,1)
  Length = 2
  Length2 = 10
  Profile = -> Sketch030
  ReferenceAxis = -> Sketch030 [N_Axis]
  Type = 0
FEATURE [Sketcher::SketchObject] Sketch031
  FullyConstrained = true
  MapMode = 5
  Support = -> [XY_Plane007]
  sketch-geometry (1):
    g0: Circle CenterX=0 CenterY=0 CenterZ=0 NormalX=0 NormalY=0 NormalZ=1 AngleXU=0 Radius=5.5
  constraints (2):
    c: Coincident(g0,g-1)
    c: Diameter(g0) = 11
FEATURE [PartDesign::Pocket] Pocket011
  BaseFeature = -> Pad016
  Direction = (0,0,-1)
  Length = 5
  Length2 = 5
  Profile = -> Sketch031
  ReferenceAxis = -> Sketch031 [N_Axis]
  Reversed = true
  Type = 1
FEATURE [Sketcher::SketchObject] Sketch032
  FullyConstrained = true
  MapMode = 5
  Support = -> [XY_Plane007]
  sketch-geometry (4):
    g0: LineSegment StartX=-1.3 StartY=8 StartZ=0 EndX=1.3 EndY=8 EndZ=0
    g1: LineSegment StartX=1.3 StartY=8 StartZ=0 EndX=1.3 EndY=-8 EndZ=0
    g2: LineSegment StartX=1.3 StartY=-8 StartZ=0 EndX=-1.3 EndY=-8 EndZ=0
    g3: LineSegment StartX=-1.3 StartY=-8 StartZ=0 EndX=-1.3 EndY=8 EndZ=0
  constraints (10):
    c: Coincident(g0,g1)
    c: Coincident(g1,g2)
    c: Coincident(g2,g3)
    c: Coincident(g3,g0)
    c: Horizontal(g2)
    c: Vertical(g1)
    c: DistanceX(g0,g0) = 2.6
    c: DistanceY(g1,g1) = 16
    c: Symmetric(g0,g2,g-1)
    c: Symmetric(g0,g0,g-2)
FEATURE [PartDesign::Pocket] Pocket012
  BaseFeature = -> Pocket011
  Direction = (0,0,-1)
  Length = 5
  Length2 = 5
  Profile = -> Sketch032
  ReferenceAxis = -> Sketch032 [N_Axis]
  Reversed = true
  Type = 1
FEATURE [Sketcher::SketchObject] Sketch033
  FullyConstrained = true
  MapMode = 5
  Support = -> [XY_Plane007]
  sketch-geometry (4):
    g0: LineSegment StartX=-8 StartY=3 StartZ=0 EndX=8 EndY=3 EndZ=0
    g1: LineSegment StartX=8 StartY=3 StartZ=0 EndX=8 EndY=-3 EndZ=0
    g2: LineSegment StartX=8 StartY=-3 StartZ=0 EndX=-8 EndY=-3 EndZ=0
    g3: LineSegment StartX=-8 StartY=-3 StartZ=0 EndX=-8 EndY=3 EndZ=0
  constraints (10):
    c: Coincident(g0,g1)
    c: Coincident(g1,g2)
    c: Coincident(g2,g3)
    c: Coincident(g3,g0)
    c: Horizontal(g2)
    c: Vertical(g1)
    c: DistanceY(g1,g1) = 6
    c: DistanceX(g0,g0) = 16
    c: Symmetric(g0,g0,g-2)
    c: Symmetric(g0,g2,g-1)
FEATURE [PartDesign::Pocket] Pocket013
  BaseFeature = -> Pocket012
  Direction = (0,0,-1)
  Length = 5
  Length2 = 5
  Profile = -> Sketch033
  ReferenceAxis = -> Sketch033 [N_Axis]
  Reversed = true
  Type = 1
FEATURE [PartDesign::Body] Washer
  Group = -> [LCS_006,Sketch030,Pad016,Sketch031,Pocket011,Sketch032,Pocket012,Sketch033,Pocket013]
  Origin = -> Origin007
  Tip = -> Pocket013
COMPONENT P5 — recipe-attached ("screw", modeled in this document).
Construction recipe (the document's own serialized feature program — sketch geometry with constraints, then the solid features built on it; lengths are millimeters unless a unit is written):

FEATURE [PartDesign::CoordinateSystem] LCS_004
  AttacherType = Attacher::AttachEngine3D
  MapMode = 2
  Support = -> [X_Axis005]
FEATURE [Sketcher::SketchObject] Sketch020
  AttachmentOffset = pos=(0,0,3) rot=(0,0,1;0rad)
  FullyConstrained = true
  MapMode = 5
  Placement = pos=(0,-3,-7e-16) rot=(1,0,0;1.5708rad)
  Support = -> [XZ_Plane005]
  sketch-geometry (4):
    g0: LineSegment StartX=-1.15 StartY=3 StartZ=0 EndX=1.15 EndY=3 EndZ=0
    g1: LineSegment StartX=1.15 StartY=3 StartZ=0 EndX=1.15 EndY=17 EndZ=0
    g2: LineSegment StartX=1.15 StartY=17 StartZ=0 EndX=-1.15 EndY=17 EndZ=0
    g3: LineSegment StartX=-1.15 StartY=17 StartZ=0 EndX=-1.15 EndY=3 EndZ=0
  constraints (11):
    c: Coincident(g0,g1)
    c: Coincident(g1,g2)
    c: Coincident(g2,g3)
    c: Coincident(g3,g0)
    c: Horizontal(g2)
    c: Vertical(g1)
    c: DistanceY(g1,g1) = -14
    c: DistanceX(g0,g0) = 2.3
    c: Symmetric(g0,g0,g-2)
    c: DistanceY(g-1,g0) = 3
    c: Vertical(g3)
FEATURE [PartDesign::Pad] Pad010
  Direction = (0,-1,-2e-16)
  Length = 3
  Length2 = 10
  Placement = pos=(0,0,0) rot=(1,0,0;1.5708rad)
  Profile = -> Sketch020
  ReferenceAxis = -> Sketch020 [N_Axis]
  Type = 0
FEATURE [Sketcher::SketchObject] Sketch021
  AttachmentOffset = pos=(0,0,3) rot=(0,0,1;0rad)
  FullyConstrained = true
  MapMode = 5
  Placement = pos=(0,-3,-7e-16) rot=(1,0,0;1.5708rad)
  Support = -> [XZ_Plane005]
  expr: Constraints[9] = -1 * (2.38 - 10) + 4.75
  sketch-geometry (4):
    g0: LineSegment StartX=-7 StartY=12.37 StartZ=0 EndX=7 EndY=12.37 EndZ=0
    g1: LineSegment StartX=7 StartY=12.37 StartZ=0 EndX=7 EndY=7.62 EndZ=0
    g2: LineSegment StartX=7 StartY=7.62 StartZ=0 EndX=-7 EndY=7.62 EndZ=0
    g3: LineSegment StartX=-7 StartY=7.62 StartZ=0 EndX=-7 EndY=12.37 EndZ=0
  constraints (11):
    c: Coincident(g0,g1)
    c: Coincident(g1,g2)
    c: Coincident(g2,g3)
    c: Coincident(g3,g0)
    c: Horizontal(g2)
    c: Vertical(g1)
    c: DistanceY(g1,g1) = 4.75
    c: DistanceX(g0,g0) = 14
    c: Symmetric(g0,g0,g-2)
    c: DistanceY(g-1,g0) = 12.37
    c: Vertical(g3)
FEATURE [Sketcher::SketchObject] Sketch022
  AttachmentOffset = pos=(0,0,3) rot=(0,0,1;0rad)
  FullyConstrained = true
  MapMode = 5
  Placement = pos=(0,-3,-7e-16) rot=(1,0,0;1.5708rad)
  Support = -> [XZ_Plane005]
  expr: Constraints[2] = 10 mm
  sketch-geometry (1):
    g0: Circle CenterX=0 CenterY=10 CenterZ=0 NormalX=0 NormalY=0 NormalZ=1 AngleXU=0 Radius=5
  constraints (3):
    c: Diameter(g0) = 10
    c: DistanceX(g-1,g0) = 0
    c: DistanceY(g-1,g0) = 10
FEATURE [PartDesign::Pad] Pad011
  BaseFeature = -> Pad010
  Direction = (0,-1,-2e-16)
  Length = 3
  Length2 = 10
  Placement = pos=(0,0,0) rot=(1,0,0;1.5708rad)
  Profile = -> Sketch021
  ReferenceAxis = -> Sketch021 [N_Axis]
  Type = 0
FEATURE [PartDesign::Pad] Pad012
  BaseFeature = -> Pad011
  Direction = (0,-1,-2e-16)
  Length = 2
  Length2 = 10
  Placement = pos=(0,0,0) rot=(1,0,0;1.5708rad)
  Profile = -> Sketch022
  ReferenceAxis = -> Sketch022 [N_Axis]
  Type = 0
FEATURE [Sketcher::SketchObject] Sketch023
  FullyConstrained = true
  MapMode = 5
  Placement = pos=(0,0,0) rot=(1,0,0;1.5708rad)
  Support = -> [XZ_Plane005]
  sketch-geometry (4):
    g0: LineSegment StartX=-7.5 StartY=25 StartZ=0 EndX=21 EndY=25 EndZ=0
    g1: LineSegment StartX=21 StartY=25 StartZ=0 EndX=21 EndY=-25 EndZ=0
    g2: LineSegment StartX=21 StartY=-25 StartZ=0 EndX=-7.5 EndY=-25 EndZ=0
    g3: LineSegment StartX=-7.5 StartY=-25 StartZ=0 EndX=-7.5 EndY=25 EndZ=0
  constraints (11):
    c: Coincident(g0,g1)
    c: Coincident(g1,g2)
    c: Coincident(g2,g3)
    c: Coincident(g3,g0)
    c: Horizontal(g2)
    c: Vertical(g1)
    c: DistanceY(g3,g3) = 50
    c: DistanceX(g0,g0) = 28.5
    c: Symmetric(g0,g2,g-1)
    c: Horizontal(g0)
    c: DistanceX(g-1,g0) = 21
FEATURE [PartDesign::Pad] Pad013
  BaseFeature = -> Pad012
  Direction = (0,-1,-2e-16)
  Length = 3
  Length2 = 10
  Placement = pos=(0,0,0) rot=(1,0,0;1.5708rad)
  Profile = -> Sketch023
  ReferenceAxis = -> Sketch023 [N_Axis]
  Type = 0
FEATURE [Sketcher::SketchObject] Sketch024
  FullyConstrained = true
  MapMode = 5
  Placement = pos=(0,0,0) rot=(1,0,0;1.5708rad)
  Support = -> [XZ_Plane005]
  sketch-geometry (4):
    g0: LineSegment StartX=16 StartY=25 StartZ=0 EndX=21 EndY=25 EndZ=0
    g1: LineSegment StartX=21 StartY=25 StartZ=0 EndX=21 EndY=-25 EndZ=0
    g2: LineSegment StartX=21 StartY=-25 StartZ=0 EndX=16 EndY=-25 EndZ=0
    g3: LineSegment StartX=16 StartY=-25 StartZ=0 EndX=16 EndY=25 EndZ=0
  constraints (11):
    c: Coincident(g0,g1)
    c: Coincident(g1,g2)
    c: Coincident(g2,g3)
    c: Coincident(g3,g0)
    c: Horizontal(g0)
    c: Horizontal(g2)
    c: Vertical(g1)
    c: DistanceX(g0,g0) = 5
    c: Symmetric(g0,g2,g-1)
    c: DistanceY(g3,g3) = 50
    c: DistanceX(g0,g-1) = -21
FEATURE [PartDesign::Pad] Pad014
  BaseFeature = -> Pad013
  Direction = (0,-1,-2e-16)
  Length = 13
  Length2 = 10
  Placement = pos=(0,0,0) rot=(1,0,0;1.5708rad)
  Profile = -> Sketch024
  ReferenceAxis = -> Sketch024 [N_Axis]
  Reversed = true
  Type = 0
FEATURE [PartDesign::SubtractiveCylinder] Cylinder003
  Angle = 360
  AttacherType = Attacher::AttachEngine3D
  AttachmentOffset = pos=(5.75,-19.5,10) rot=(0,0,1;0rad)
  BaseFeature = -> Pad014
  FirstAngle = 0
  Height = 15
  MapMode = 5
  Placement = pos=(10,5.75,-19.5) rot=(0.57735,0.57735,0.57735;2.0944rad)
  Radius = 2
  SecondAngle = 0
  Support = -> [YZ_Plane005]
FEATURE [PartDesign::Mirrored] Mirrored011
  BaseFeature = -> Cylinder003
  MirrorPlane = -> XY_Plane005
  Originals = -> [Cylinder003]
  Placement = pos=(10,5.75,-19.5) rot=(0.57735,0.57735,0.57735;2.0944rad)
FEATURE [PartDesign::Chamfer] Chamfer001
  Angle = 45
  Base = -> Mirrored011 [Edge37,Edge38]
  BaseFeature = -> Mirrored011
  ChamferType = 0
  FlipDirection = false
  Placement = pos=(10,5.75,-19.5) rot=(0.57735,0.57735,0.57735;2.0944rad)
  Size = 1.5
  Size2 = 1
  SupportTransform = false
  UseAllEdges = false
FEATURE [PartDesign::Body] screw
  Group = -> [LCS_004,Sketch020,Pad010,Sketch021,Sketch022,Pad011,Pad012,Sketch023,Pad013,Sketch024,Pad014,Cylinder003,Mirrored011,Chamfer001]
  Origin = -> Origin005
  Tip = -> Chamfer001
PROVENANCE & LICENSES
A FreeCAD (.FCStd) document from a public repository crawl; recipes are the document's own serialized feature recipes (and, for linked parts, companion documents' recipes).
License: as declared in the source repository (recorded in the dataset sidecar).
